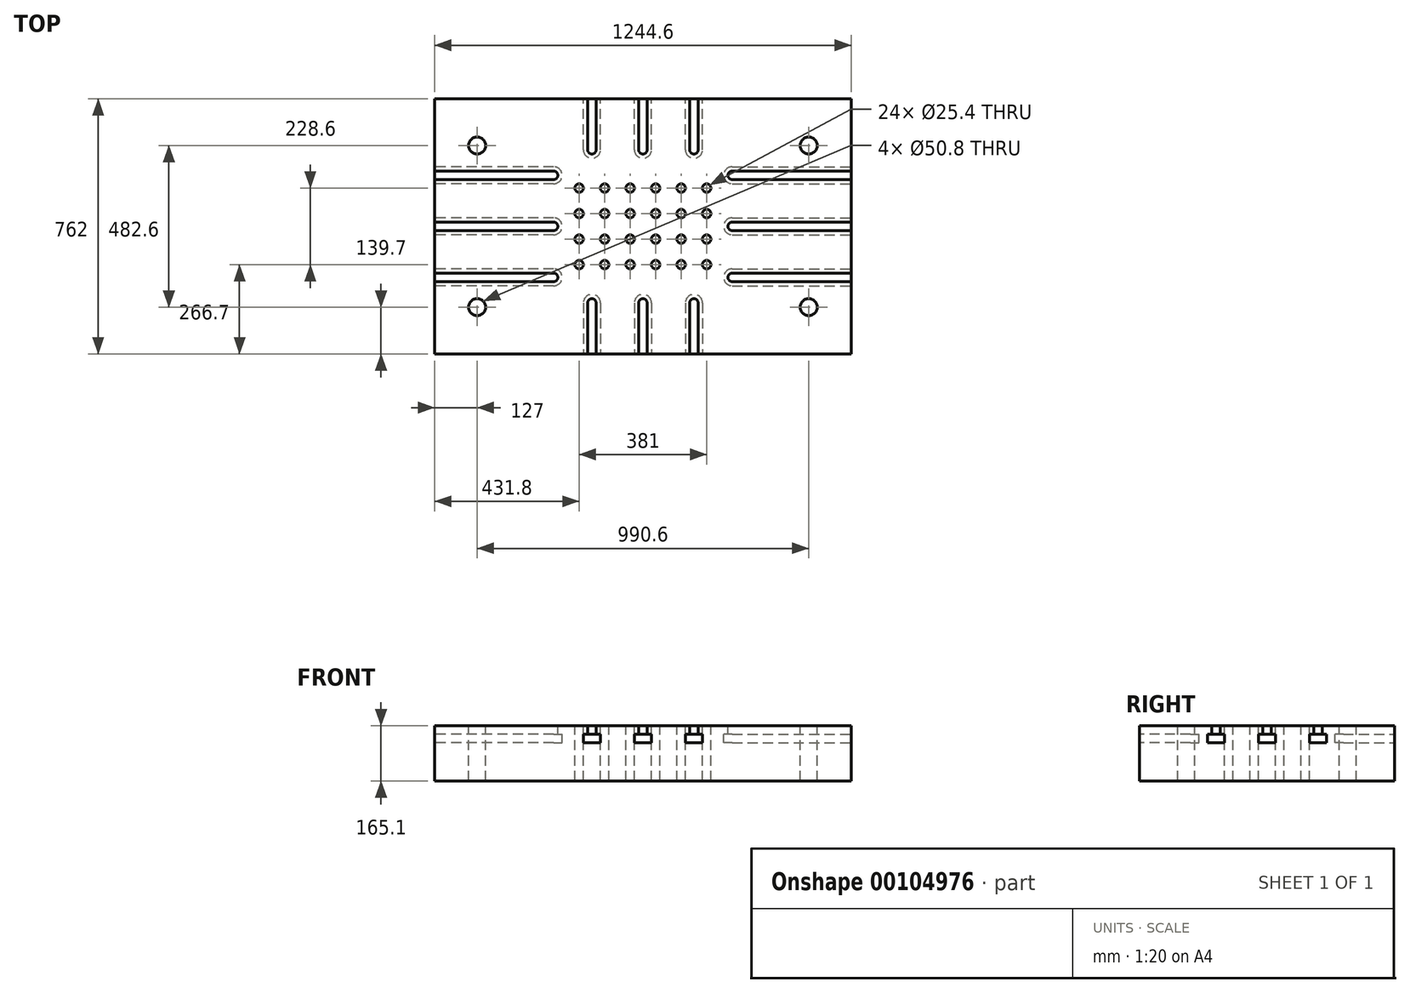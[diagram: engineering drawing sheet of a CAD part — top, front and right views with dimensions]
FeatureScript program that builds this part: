
annotation { "Feature Type Name" : "Feature", "Feature Type Description" : "" }
export const myFeature = defineFeature(function(context is Context, id is Id, definition is map)
    precondition{}
    {
        {
            var Q0;
            Q0=qCreatedBy(makeId("Top.planeOp"),FACE);
            var sketch = newSketch(context, id + "F0", { "sketchPlane" : qUnion([Q0])});
            skLineSegment(sketch, "E0.bottom", {"start": v(0, 0) * mm, "end": v(1244.6, 0) * mm});
            skLineSegment(sketch, "E0.top", {"start": v(0, 762) * mm, "end": v(1244.6, 762) * mm});
            skLineSegment(sketch, "E0.left", {"start": v(0, 0) * mm, "end": v(0, 762) * mm});
            skLineSegment(sketch, "E0.right", {"start": v(1244.6, 0) * mm, "end": v(1244.6, 762) * mm});
            skSolve(sketch);
        }
        {
            var Q0;
            Q0 = qSketchRegion(id + "F0", true);
            extrude(context, id + "F1", {"entities" : qUnion([Q0]), "oppositeDirection" : true, "depth" : 165.1 * mm});
        }
        {
            var Q0;
            Q0=makeQuery(id+"F1.opExtrude","SWEPT_FACE",FACE,{"disambiguationData":[OSD([sQuery(id+"F0.wireOp",EDGE,"E0.bottom")])]});
            var sketch = newSketch(context, id + "F2", { "sketchPlane" : qUnion([Q0])});
            skLineSegment(sketch, "E1", {"start": v(444.5, -25.4) * mm, "end": v(444.5, -50.8) * mm});
            skLineSegment(sketch, "E2", {"start": v(444.5, -50.8) * mm, "end": v(495.3, -50.8) * mm});
            skLineSegment(sketch, "E3", {"start": v(495.3, -50.8) * mm, "end": v(495.3, -25.4) * mm});
            skLineSegment(sketch, "E4", {"start": v(495.3, -25.4) * mm, "end": v(482.6, -25.4) * mm});
            skLineSegment(sketch, "E5", {"start": v(482.6, -25.4) * mm, "end": v(482.6, 0) * mm});
            skLineSegment(sketch, "E6", {"start": v(444.5, -25.4) * mm, "end": v(457.2, -25.4) * mm});
            skLineSegment(sketch, "E7", {"start": v(457.2, -25.4) * mm, "end": v(457.2, 0) * mm});
            skLineSegment(sketch, "E8", {"start": v(596.9, -25.4) * mm, "end": v(596.9, -50.8) * mm});
            skLineSegment(sketch, "E9", {"start": v(596.9, -50.8) * mm, "end": v(647.7, -50.8) * mm});
            skLineSegment(sketch, "E10", {"start": v(647.7, -50.8) * mm, "end": v(647.7, -25.4) * mm});
            skLineSegment(sketch, "E11", {"start": v(647.7, -25.4) * mm, "end": v(635, -25.4) * mm});
            skLineSegment(sketch, "E12", {"start": v(635, -25.4) * mm, "end": v(635, 0) * mm});
            skLineSegment(sketch, "E13", {"start": v(596.9, -25.4) * mm, "end": v(609.6, -25.4) * mm});
            skLineSegment(sketch, "E14", {"start": v(609.6, -25.4) * mm, "end": v(609.6, 0) * mm});
            skLineSegment(sketch, "E15", {"start": v(749.3, -25.4) * mm, "end": v(749.3, -50.8) * mm});
            skLineSegment(sketch, "E16", {"start": v(749.3, -50.8) * mm, "end": v(800.1, -50.8) * mm});
            skLineSegment(sketch, "E17", {"start": v(800.1, -50.8) * mm, "end": v(800.1, -25.4) * mm});
            skLineSegment(sketch, "E18", {"start": v(800.1, -25.4) * mm, "end": v(787.4, -25.4) * mm});
            skLineSegment(sketch, "E19", {"start": v(787.4, -25.4) * mm, "end": v(787.4, 0) * mm});
            skLineSegment(sketch, "E20", {"start": v(749.3, -25.4) * mm, "end": v(762, -25.4) * mm});
            skLineSegment(sketch, "E21", {"start": v(762, -25.4) * mm, "end": v(762, 0) * mm});
            skSolve(sketch);
        }
        {
            var Q0;
            Q0 = qSketchRegion(id + "F2", true);
            var Q1;
            Q1=makeQuery(id+"F2.imprint","IMPRINT",FACE,{"disambiguationData":[TD([[makeQuery(id+"F2.imprint","IMPRINT",EDGE,{"derivedFrom":sQuery(id+"F2.wireOp",EDGE,"E1")}),1.0]])]});
            var Q2;
            Q2=makeQuery(id+"F2.imprint","IMPRINT",FACE,{"disambiguationData":[TD([[makeQuery(id+"F2.imprint","IMPRINT",EDGE,{"derivedFrom":sQuery(id+"F2.wireOp",EDGE,"E8")}),1.0]])]});
            var Q3;
            Q3=makeQuery(id+"F2.imprint","IMPRINT",FACE,{"disambiguationData":[TD([[makeQuery(id+"F2.imprint","IMPRINT",EDGE,{"derivedFrom":sQuery(id+"F2.wireOp",EDGE,"E15")}),1.0]])]});
            extrude(context, id + "F3", {"entities" : qUnion([Q0, Q1, Q2, Q3]), "operationType" : NewBodyOperationType.REMOVE, "oppositeDirection" : true, "depth" : 152.4 * mm});
        }
        {
            var Q0;
            Q0=makeQuery(id+"F1.opExtrude","SWEPT_FACE",FACE,{"disambiguationData":[OSD([sQuery(id+"F0.wireOp",EDGE,"E0.right")])]});
            var sketch = newSketch(context, id + "F4", { "sketchPlane" : qUnion([Q0])});
            skLineSegment(sketch, "E22", {"start": v(215.9, 0) * mm, "end": v(215.9, -25.4) * mm});
            skLineSegment(sketch, "E23", {"start": v(215.9, -25.4) * mm, "end": v(203.2, -25.4) * mm});
            skLineSegment(sketch, "E24", {"start": v(203.2, -25.4) * mm, "end": v(203.2, -50.8) * mm});
            skLineSegment(sketch, "E25", {"start": v(203.2, -50.8) * mm, "end": v(254, -50.8) * mm});
            skLineSegment(sketch, "E26", {"start": v(254, -50.8) * mm, "end": v(254, -25.4) * mm});
            skLineSegment(sketch, "E27", {"start": v(254, -25.4) * mm, "end": v(241.3, -25.4) * mm});
            skLineSegment(sketch, "E28", {"start": v(241.3, -25.4) * mm, "end": v(241.3, 0) * mm});
            skLineSegment(sketch, "E29", {"start": v(368.3, 0) * mm, "end": v(368.3, -25.4) * mm});
            skLineSegment(sketch, "E30", {"start": v(368.3, -25.4) * mm, "end": v(355.6, -25.4) * mm});
            skLineSegment(sketch, "E31", {"start": v(355.6, -25.4) * mm, "end": v(355.6, -50.8) * mm});
            skLineSegment(sketch, "E32", {"start": v(355.6, -50.8) * mm, "end": v(406.4, -50.8) * mm});
            skLineSegment(sketch, "E33", {"start": v(406.4, -50.8) * mm, "end": v(406.4, -25.4) * mm});
            skLineSegment(sketch, "E34", {"start": v(406.4, -25.4) * mm, "end": v(393.7, -25.4) * mm});
            skLineSegment(sketch, "E35", {"start": v(393.7, -25.4) * mm, "end": v(393.7, 0) * mm});
            skLineSegment(sketch, "E36", {"start": v(520.7, 0) * mm, "end": v(520.7, -25.4) * mm});
            skLineSegment(sketch, "E37", {"start": v(520.7, -25.4) * mm, "end": v(508, -25.4) * mm});
            skLineSegment(sketch, "E38", {"start": v(508, -25.4) * mm, "end": v(508, -50.8) * mm});
            skLineSegment(sketch, "E39", {"start": v(508, -50.8) * mm, "end": v(558.8, -50.8) * mm});
            skLineSegment(sketch, "E40", {"start": v(558.8, -50.8) * mm, "end": v(558.8, -25.4) * mm});
            skLineSegment(sketch, "E41", {"start": v(558.8, -25.4) * mm, "end": v(546.1, -25.4) * mm});
            skLineSegment(sketch, "E42", {"start": v(546.1, -25.4) * mm, "end": v(546.1, 0) * mm});
            skLineSegment(sketch, "E43", {"start": v(215.9, 0) * mm, "end": v(0, 0) * mm});
            skLineSegment(sketch, "E44", {"start": v(546.1, 0) * mm, "end": v(762, 0) * mm});
            skSolve(sketch);
        }
        {
            var Q0;
            Q0 = qSketchRegion(id + "F4", true);
            var Q1;
            {var subQ1=sQuery(id+"F4.wireOp",EDGE,"E22");Q1=makeQuery(id+"F4.imprint","IMPRINT",FACE,{"disambiguationData":[TD([[makeQuery(id+"F4.imprint","IMPRINT",EDGE,{"derivedFrom":subQ1}),1.0]])]});}
            var Q2;
            {var subQ0=sQuery(id+"F4.wireOp",EDGE,"E29");Q2=makeQuery(id+"F4.imprint","IMPRINT",FACE,{"disambiguationData":[TD([[makeQuery(id+"F4.imprint","IMPRINT",EDGE,{"derivedFrom":subQ0}),1.0]])]});}
            var Q3;
            {var subQ1=sQuery(id+"F4.wireOp",EDGE,"E36");Q3=makeQuery(id+"F4.imprint","IMPRINT",FACE,{"disambiguationData":[TD([[makeQuery(id+"F4.imprint","IMPRINT",EDGE,{"derivedFrom":subQ1}),1.0]])]});}
            extrude(context, id + "F5", {"entities" : qUnion([Q0, Q1, Q2, Q3]), "operationType" : NewBodyOperationType.REMOVE, "oppositeDirection" : true, "depth" : 355.6 * mm});
        }
        {
            var Q0;
            Q0=makeQuery(id+"F1.opExtrude","SWEPT_FACE",FACE,{"disambiguationData":[OSD([sQuery(id+"F0.wireOp",EDGE,"E0.left")])]});
            var sketch = newSketch(context, id + "F6", { "sketchPlane" : qUnion([Q0])});
            skLineSegment(sketch, "E45", {"start": v(-546.1, 0) * mm, "end": v(-546.1, -25.4) * mm});
            skLineSegment(sketch, "E46", {"start": v(-546.1, -25.4) * mm, "end": v(-558.8, -25.4) * mm});
            skLineSegment(sketch, "E47", {"start": v(-558.8, -25.4) * mm, "end": v(-558.8, -50.8) * mm});
            skLineSegment(sketch, "E48", {"start": v(-558.8, -50.8) * mm, "end": v(-508, -50.8) * mm});
            skLineSegment(sketch, "E49", {"start": v(-508, -50.8) * mm, "end": v(-508, -25.4) * mm});
            skLineSegment(sketch, "E50", {"start": v(-508, -25.4) * mm, "end": v(-520.7, -25.4) * mm});
            skLineSegment(sketch, "E51", {"start": v(-520.7, -25.4) * mm, "end": v(-520.7, 0) * mm});
            skLineSegment(sketch, "E52", {"start": v(-520.7, 0) * mm, "end": v(-546.1, 0) * mm});
            skLineSegment(sketch, "E53", {"start": v(-393.7, 0) * mm, "end": v(-393.7, -25.4) * mm});
            skLineSegment(sketch, "E54", {"start": v(-393.7, -25.4) * mm, "end": v(-406.4, -25.4) * mm});
            skLineSegment(sketch, "E55", {"start": v(-406.4, -25.4) * mm, "end": v(-406.4, -50.8) * mm});
            skLineSegment(sketch, "E56", {"start": v(-406.4, -50.8) * mm, "end": v(-355.6, -50.8) * mm});
            skLineSegment(sketch, "E57", {"start": v(-355.6, -50.8) * mm, "end": v(-355.6, -25.4) * mm});
            skLineSegment(sketch, "E58", {"start": v(-355.6, -25.4) * mm, "end": v(-368.3, -25.4) * mm});
            skLineSegment(sketch, "E59", {"start": v(-368.3, -25.4) * mm, "end": v(-368.3, 0) * mm});
            skLineSegment(sketch, "E60", {"start": v(-368.3, 0) * mm, "end": v(-393.7, 0) * mm});
            skLineSegment(sketch, "E61", {"start": v(-241.3, 0) * mm, "end": v(-241.3, -25.4) * mm});
            skLineSegment(sketch, "E62", {"start": v(-241.3, -25.4) * mm, "end": v(-254, -25.4) * mm});
            skLineSegment(sketch, "E63", {"start": v(-254, -25.4) * mm, "end": v(-254, -50.8) * mm});
            skLineSegment(sketch, "E64", {"start": v(-254, -50.8) * mm, "end": v(-203.2, -50.8) * mm});
            skLineSegment(sketch, "E65", {"start": v(-203.2, -50.8) * mm, "end": v(-203.2, -25.4) * mm});
            skLineSegment(sketch, "E66", {"start": v(-203.2, -25.4) * mm, "end": v(-215.9, -25.4) * mm});
            skLineSegment(sketch, "E67", {"start": v(-215.9, -25.4) * mm, "end": v(-215.9, 0) * mm});
            skLineSegment(sketch, "E68", {"start": v(-215.9, 0) * mm, "end": v(-241.3, 0) * mm});
            skLineSegment(sketch, "E69", {"start": v(-546.1, 0) * mm, "end": v(-762, 0) * mm});
            skLineSegment(sketch, "E70", {"start": v(-215.9, 0) * mm, "end": v(0, 0) * mm});
            skSolve(sketch);
        }
        {
            var Q0;
            Q0 = qSketchRegion(id + "F6", true);
            extrude(context, id + "F7", {"entities" : qUnion([Q0]), "operationType" : NewBodyOperationType.REMOVE, "oppositeDirection" : true, "depth" : 355.6 * mm});
        }
        {
            var Q0;
            Q0=makeQuery(id+"F1.opExtrude","SWEPT_FACE",FACE,{"disambiguationData":[OSD([sQuery(id+"F0.wireOp",EDGE,"E0.top")])]});
            var sketch = newSketch(context, id + "F8", { "sketchPlane" : qUnion([Q0])});
            skLineSegment(sketch, "E71", {"start": v(-787.4, 0) * mm, "end": v(-787.4, -25.4) * mm});
            skLineSegment(sketch, "E72", {"start": v(-787.4, -25.4) * mm, "end": v(-800.1, -25.4) * mm});
            skLineSegment(sketch, "E73", {"start": v(-800.1, -25.4) * mm, "end": v(-800.1, -50.8) * mm});
            skLineSegment(sketch, "E74", {"start": v(-800.1, -50.8) * mm, "end": v(-749.3, -50.8) * mm});
            skLineSegment(sketch, "E75", {"start": v(-749.3, -50.8) * mm, "end": v(-749.3, -25.4) * mm});
            skLineSegment(sketch, "E76", {"start": v(-749.3, -25.4) * mm, "end": v(-762, -25.4) * mm});
            skLineSegment(sketch, "E77", {"start": v(-762, -25.4) * mm, "end": v(-762, 0) * mm});
            skLineSegment(sketch, "E78", {"start": v(-762, 0) * mm, "end": v(-787.4, 0) * mm});
            skLineSegment(sketch, "E79", {"start": v(-635, 0) * mm, "end": v(-635, -25.4) * mm});
            skLineSegment(sketch, "E80", {"start": v(-635, -25.4) * mm, "end": v(-647.7, -25.4) * mm});
            skLineSegment(sketch, "E81", {"start": v(-647.7, -25.4) * mm, "end": v(-647.7, -50.8) * mm});
            skLineSegment(sketch, "E82", {"start": v(-647.7, -50.8) * mm, "end": v(-596.9, -50.8) * mm});
            skLineSegment(sketch, "E83", {"start": v(-596.9, -50.8) * mm, "end": v(-596.9, -25.4) * mm});
            skLineSegment(sketch, "E84", {"start": v(-596.9, -25.4) * mm, "end": v(-609.6, -25.4) * mm});
            skLineSegment(sketch, "E85", {"start": v(-609.6, -25.4) * mm, "end": v(-609.6, 0) * mm});
            skLineSegment(sketch, "E86", {"start": v(-609.6, 0) * mm, "end": v(-635, 0) * mm});
            skLineSegment(sketch, "E87", {"start": v(-482.6, 0) * mm, "end": v(-482.6, -25.4) * mm});
            skLineSegment(sketch, "E88", {"start": v(-482.6, -25.4) * mm, "end": v(-495.3, -25.4) * mm});
            skLineSegment(sketch, "E89", {"start": v(-495.3, -25.4) * mm, "end": v(-495.3, -50.8) * mm});
            skLineSegment(sketch, "E90", {"start": v(-495.3, -50.8) * mm, "end": v(-444.5, -50.8) * mm});
            skLineSegment(sketch, "E91", {"start": v(-444.5, -50.8) * mm, "end": v(-444.5, -25.4) * mm});
            skLineSegment(sketch, "E92", {"start": v(-444.5, -25.4) * mm, "end": v(-457.2, -25.4) * mm});
            skLineSegment(sketch, "E93", {"start": v(-457.2, -25.4) * mm, "end": v(-457.2, 0) * mm});
            skLineSegment(sketch, "E94", {"start": v(-457.2, 0) * mm, "end": v(-482.6, 0) * mm});
            skSolve(sketch);
        }
        {
            var Q0;
            Q0 = qSketchRegion(id + "F8", true);
            extrude(context, id + "F9", {"entities" : qUnion([Q0]), "operationType" : NewBodyOperationType.REMOVE, "oppositeDirection" : true, "depth" : 152.4 * mm});
        }
        {
            var Q0;
            Q0=makeQuery(id+"F1.opExtrude","CAP_FACE",FACE,{"disambiguationData":[OSD([sQuery(id+"F0.wireOp",EDGE,"E0.bottom"),sQuery(id+"F0.wireOp",EDGE,"E0.top"),sQuery(id+"F0.wireOp",EDGE,"E0.left"),sQuery(id+"F0.wireOp",EDGE,"E0.right")])],"isStart":true});
            var sketch = newSketch(context, id + "F10", { "sketchPlane" : qUnion([Q0])});
            skLineSegment(sketch, "E95.0", {"start": v(457.2, 609.6) * mm, "end": v(482.6, 609.6) * mm});
            skLineSegment(sketch, "E95.1", {"start": v(609.6, 609.6) * mm, "end": v(635, 609.6) * mm});
            skLineSegment(sketch, "E95.2", {"start": v(762, 609.6) * mm, "end": v(787.4, 609.6) * mm});
            skLineSegment(sketch, "E95.27", {"start": v(889, 520.7) * mm, "end": v(889, 546.1) * mm});
            skLineSegment(sketch, "E95.28", {"start": v(889, 368.3) * mm, "end": v(889, 393.7) * mm});
            skLineSegment(sketch, "E95.29", {"start": v(889, 215.9) * mm, "end": v(889, 241.3) * mm});
            skLineSegment(sketch, "E95.31", {"start": v(355.6, 368.3) * mm, "end": v(355.6, 393.7) * mm});
            skLineSegment(sketch, "E95.32", {"start": v(355.6, 241.3) * mm, "end": v(355.6, 241.3) * mm});
            skLineSegment(sketch, "E95.33", {"start": v(457.2, 152.4) * mm, "end": v(482.6, 152.4) * mm});
            skLineSegment(sketch, "E95.34", {"start": v(609.6, 152.4) * mm, "end": v(635, 152.4) * mm});
            skLineSegment(sketch, "E95.35", {"start": v(762, 152.4) * mm, "end": v(787.4, 152.4) * mm});
            skCircle(sketch, "E96", {"center": v(622.3, 609.6) * mm, "radius": 12.7 * mm});
            skCircle(sketch, "E97", {"center": v(774.7, 609.6) * mm, "radius": 12.7 * mm});
            skCircle(sketch, "E98", {"center": v(469.9, 609.6) * mm, "radius": 12.7 * mm});
            skCircle(sketch, "E99", {"center": v(355.6, 381) * mm, "radius": 12.7 * mm});
            skCircle(sketch, "E100", {"center": v(889, 381) * mm, "radius": 12.7 * mm});
            skCircle(sketch, "E101", {"center": v(774.7, 152.4) * mm, "radius": 12.7 * mm});
            skCircle(sketch, "E102", {"center": v(622.3, 152.4) * mm, "radius": 12.7 * mm});
            skCircle(sketch, "E103", {"center": v(469.9, 152.4) * mm, "radius": 12.7 * mm});
            skCircle(sketch, "E104", {"center": v(889, 228.6) * mm, "radius": 12.7 * mm});
            skCircle(sketch, "E105", {"center": v(355.6, 533.4) * mm, "radius": 12.7 * mm});
            skCircle(sketch, "E106", {"center": v(355.6, 228.6) * mm, "radius": 12.7 * mm});
            skCircle(sketch, "E107", {"center": v(889, 533.4) * mm, "radius": 12.7 * mm});
            skSolve(sketch);
        }
        {
            var Q0;
            Q0 = qSketchRegion(id + "F10", true);
            extrude(context, id + "F11", {"entities" : qUnion([Q0]), "operationType" : NewBodyOperationType.REMOVE, "oppositeDirection" : true, "depth" : 50.8 * mm});
        }
        {
            var Q0;
            Q0=makeQuery(id+"F1.opExtrude","CAP_FACE",FACE,{"disambiguationData":[OSD([sQuery(id+"F0.wireOp",EDGE,"E0.bottom"),sQuery(id+"F0.wireOp",EDGE,"E0.top"),sQuery(id+"F0.wireOp",EDGE,"E0.left"),sQuery(id+"F0.wireOp",EDGE,"E0.right")])],"isStart":true});
            var sketch = newSketch(context, id + "F12", { "sketchPlane" : qUnion([Q0])});
            skCircle(sketch, "E108", {"center": v(431.8, 495.3) * mm, "radius": 12.7 * mm});
            skCircle(sketch, "E109", {"center": v(508, 495.3) * mm, "radius": 12.7 * mm});
            skCircle(sketch, "E110", {"center": v(584.2, 495.3) * mm, "radius": 12.7 * mm});
            skCircle(sketch, "E111", {"center": v(660.4, 495.3) * mm, "radius": 12.7 * mm});
            skCircle(sketch, "E112", {"center": v(736.6, 495.3) * mm, "radius": 12.7 * mm});
            skCircle(sketch, "E113", {"center": v(812.8, 495.3) * mm, "radius": 12.7 * mm});
            skCircle(sketch, "E114", {"center": v(431.8, 419.1) * mm, "radius": 12.7 * mm});
            skCircle(sketch, "E115", {"center": v(508, 419.1) * mm, "radius": 12.7 * mm});
            skCircle(sketch, "E116", {"center": v(584.2, 419.1) * mm, "radius": 12.7 * mm});
            skCircle(sketch, "E117", {"center": v(660.4, 419.1) * mm, "radius": 12.7 * mm});
            skCircle(sketch, "E118", {"center": v(736.6, 419.1) * mm, "radius": 12.7 * mm});
            skCircle(sketch, "E119", {"center": v(812.8, 419.1) * mm, "radius": 12.7 * mm});
            skLineSegment(sketch, "E120", {"start": v(812.8, 495.3) * mm, "end": v(1244.6, 495.3) * mm});
            skLineSegment(sketch, "E121", {"start": v(431.8, 495.3) * mm, "end": v(0, 495.3) * mm});
            skCircle(sketch, "E122", {"center": v(431.8, 342.9) * mm, "radius": 12.7 * mm});
            skCircle(sketch, "E123", {"center": v(508, 342.9) * mm, "radius": 12.7 * mm});
            skCircle(sketch, "E124", {"center": v(584.2, 342.9) * mm, "radius": 12.7 * mm});
            skCircle(sketch, "E125", {"center": v(660.4, 342.9) * mm, "radius": 12.7 * mm});
            skCircle(sketch, "E126", {"center": v(736.6, 342.9) * mm, "radius": 12.7 * mm});
            skCircle(sketch, "E127", {"center": v(812.8, 342.9) * mm, "radius": 12.7 * mm});
            skCircle(sketch, "E128", {"center": v(431.8, 266.7) * mm, "radius": 12.7 * mm});
            skCircle(sketch, "E129", {"center": v(508, 266.7) * mm, "radius": 12.7 * mm});
            skCircle(sketch, "E130", {"center": v(584.2, 266.7) * mm, "radius": 12.7 * mm});
            skCircle(sketch, "E131", {"center": v(660.4, 266.7) * mm, "radius": 12.7 * mm});
            skCircle(sketch, "E132", {"center": v(736.6, 266.7) * mm, "radius": 12.7 * mm});
            skCircle(sketch, "E133", {"center": v(812.8, 266.7) * mm, "radius": 12.7 * mm});
            skLineSegment(sketch, "E134", {"start": v(812.8, 266.7) * mm, "end": v(812.8, 0) * mm});
            skLineSegment(sketch, "E135", {"start": v(812.8, 495.3) * mm, "end": v(812.8, 762) * mm});
            skSolve(sketch);
        }
        {
            var Q0;
            Q0 = qSketchRegion(id + "F12", true);
            extrude(context, id + "F13", {"entities" : qUnion([Q0]), "operationType" : NewBodyOperationType.REMOVE, "endBound" : BoundingType.THROUGH_ALL, "oppositeDirection" : true, "depth" : 25.4 * mm});
        }
        {
            var Q0;
            Q0=makeQuery(id+"F1.opExtrude","CAP_FACE",FACE,{"disambiguationData":[OSD([sQuery(id+"F0.wireOp",EDGE,"E0.bottom"),sQuery(id+"F0.wireOp",EDGE,"E0.top"),sQuery(id+"F0.wireOp",EDGE,"E0.left"),sQuery(id+"F0.wireOp",EDGE,"E0.right")])],"isStart":true});
            cPlane(context, id + "F14", {"entities" : qUnion([Q0]), "cplaneType" : CPlaneType.OFFSET, "offset" : 25.4 * mm, "oppositeDirection" : true, "width" : 152.4 * mm, "height" : 152.4 * mm});
        }
        {
            var Q0;
            Q0=qCreatedBy(id+"F14.planeOp",FACE);
            var sketch = newSketch(context, id + "F15", { "sketchPlane" : qUnion([Q0])});
            skLineSegment(sketch, "E136.0", {"start": v(749.3, 152.4) * mm, "end": v(749.3, 0) * mm});
            skLineSegment(sketch, "E137.0", {"start": v(800.1, 152.4) * mm, "end": v(800.1, 0) * mm});
            skArc(sketch, "E138.0", {"start": v(787.4, 152.4) * mm, "mid": v(774.7, 165.1) * mm, "end": v(762, 152.4) * mm});
            skPoint(sketch, "E139.first.point", {"position": v(749.3, 139.7) * mm});
            skPoint(sketch, "E139.second.point", {"position": v(774.7, 165.1) * mm});
            skPoint(sketch, "E139.third.point", {"position": v(800.1, 139.7) * mm});
            skCircle(sketch, "E140", {"center": v(774.7, 152.4) * mm, "radius": 25.4 * mm});
            skArc(sketch, "E141.0", {"start": v(482.6, 152.4) * mm, "mid": v(469.9, 165.1) * mm, "end": v(457.2, 152.4) * mm});
            skArc(sketch, "E141.1", {"start": v(635, 152.4) * mm, "mid": v(622.3, 165.1) * mm, "end": v(609.6, 152.4) * mm});
            skArc(sketch, "E141.2", {"start": v(889, 241.3) * mm, "mid": v(876.3, 228.6) * mm, "end": v(889, 215.9) * mm});
            skArc(sketch, "E141.3", {"start": v(889, 393.7) * mm, "mid": v(876.3, 381) * mm, "end": v(889, 368.3) * mm});
            skArc(sketch, "E141.5", {"start": v(355.6, 368.3) * mm, "mid": v(368.3, 381) * mm, "end": v(355.6, 393.7) * mm});
            skArc(sketch, "E141.8", {"start": v(762, 609.6) * mm, "mid": v(774.7, 596.9) * mm, "end": v(787.4, 609.6) * mm});
            skArc(sketch, "E141.9", {"start": v(609.6, 609.6) * mm, "mid": v(622.3, 596.9) * mm, "end": v(635, 609.6) * mm});
            skArc(sketch, "E141.10", {"start": v(457.2, 609.6) * mm, "mid": v(469.9, 596.9) * mm, "end": v(482.6, 609.6) * mm});
            skCircle(sketch, "E142", {"center": v(622.3, 152.4) * mm, "radius": 25.4 * mm});
            skCircle(sketch, "E143", {"center": v(469.9, 152.4) * mm, "radius": 25.4 * mm});
            skCircle(sketch, "E144", {"center": v(355.6, 381) * mm, "radius": 25.4 * mm});
            skCircle(sketch, "E145", {"center": v(889, 381) * mm, "radius": 25.4 * mm});
            skCircle(sketch, "E146", {"center": v(889, 228.6) * mm, "radius": 25.4 * mm});
            skCircle(sketch, "E147", {"center": v(774.7, 609.6) * mm, "radius": 25.4 * mm});
            skCircle(sketch, "E148", {"center": v(622.3, 609.6) * mm, "radius": 25.4 * mm});
            skCircle(sketch, "E149", {"center": v(469.9, 609.6) * mm, "radius": 25.4 * mm});
            skArc(sketch, "E150.0", {"start": v(889, 546.1) * mm, "mid": v(876.3, 533.4) * mm, "end": v(889, 520.7) * mm});
            skArc(sketch, "E150.1", {"start": v(355.6, 215.9) * mm, "mid": v(368.3, 228.6) * mm, "end": v(355.6, 241.3) * mm});
            skArc(sketch, "E150.2", {"start": v(355.6, 520.7) * mm, "mid": v(368.3, 533.4) * mm, "end": v(355.6, 546.1) * mm});
            skCircle(sketch, "E151", {"center": v(889, 533.4) * mm, "radius": 25.4 * mm});
            skCircle(sketch, "E152", {"center": v(355.6, 228.6) * mm, "radius": 25.4 * mm});
            skCircle(sketch, "E153", {"center": v(355.6, 533.4) * mm, "radius": 25.4 * mm});
            skSolve(sketch);
        }
        {
            var Q0;
            Q0 = qSketchRegion(id + "F15", true);
            extrude(context, id + "F16", {"entities" : qUnion([Q0]), "operationType" : NewBodyOperationType.REMOVE, "oppositeDirection" : true, "depth" : 25.4 * mm});
        }
        {
            var Q0;
            Q0=makeQuery(id+"F1.opExtrude","CAP_FACE",FACE,{"disambiguationData":[OSD([sQuery(id+"F0.wireOp",EDGE,"E0.bottom"),sQuery(id+"F0.wireOp",EDGE,"E0.top"),sQuery(id+"F0.wireOp",EDGE,"E0.left"),sQuery(id+"F0.wireOp",EDGE,"E0.right")])],"isStart":true});
            var sketch = newSketch(context, id + "F17", { "sketchPlane" : qUnion([Q0])});
            skCircle(sketch, "E154", {"center": v(127, 622.3) * mm, "radius": 25.4 * mm});
            skLineSegment(sketch, "E155", {"start": v(622.3, 609.6) * mm, "end": v(622.3, 152.4) * mm});
            skCircle(sketch, "E156.MirrorC", {"center": v(1117.6, 622.3) * mm, "radius": 25.4 * mm});
            skLineSegment(sketch, "E157", {"start": v(355.6, 381) * mm, "end": v(889, 381) * mm});
            skCircle(sketch, "E158.MirrorC", {"center": v(127, 139.7) * mm, "radius": 25.4 * mm});
            skCircle(sketch, "E159.MirrorC", {"center": v(1117.6, 139.7) * mm, "radius": 25.4 * mm});
            skSolve(sketch);
        }
        {
            var Q0;
            Q0 = qSketchRegion(id + "F17", true);
            extrude(context, id + "F18", {"entities" : qUnion([Q0]), "operationType" : NewBodyOperationType.REMOVE, "endBound" : BoundingType.THROUGH_ALL, "oppositeDirection" : true, "depth" : 25.4 * mm});
        }
    });
